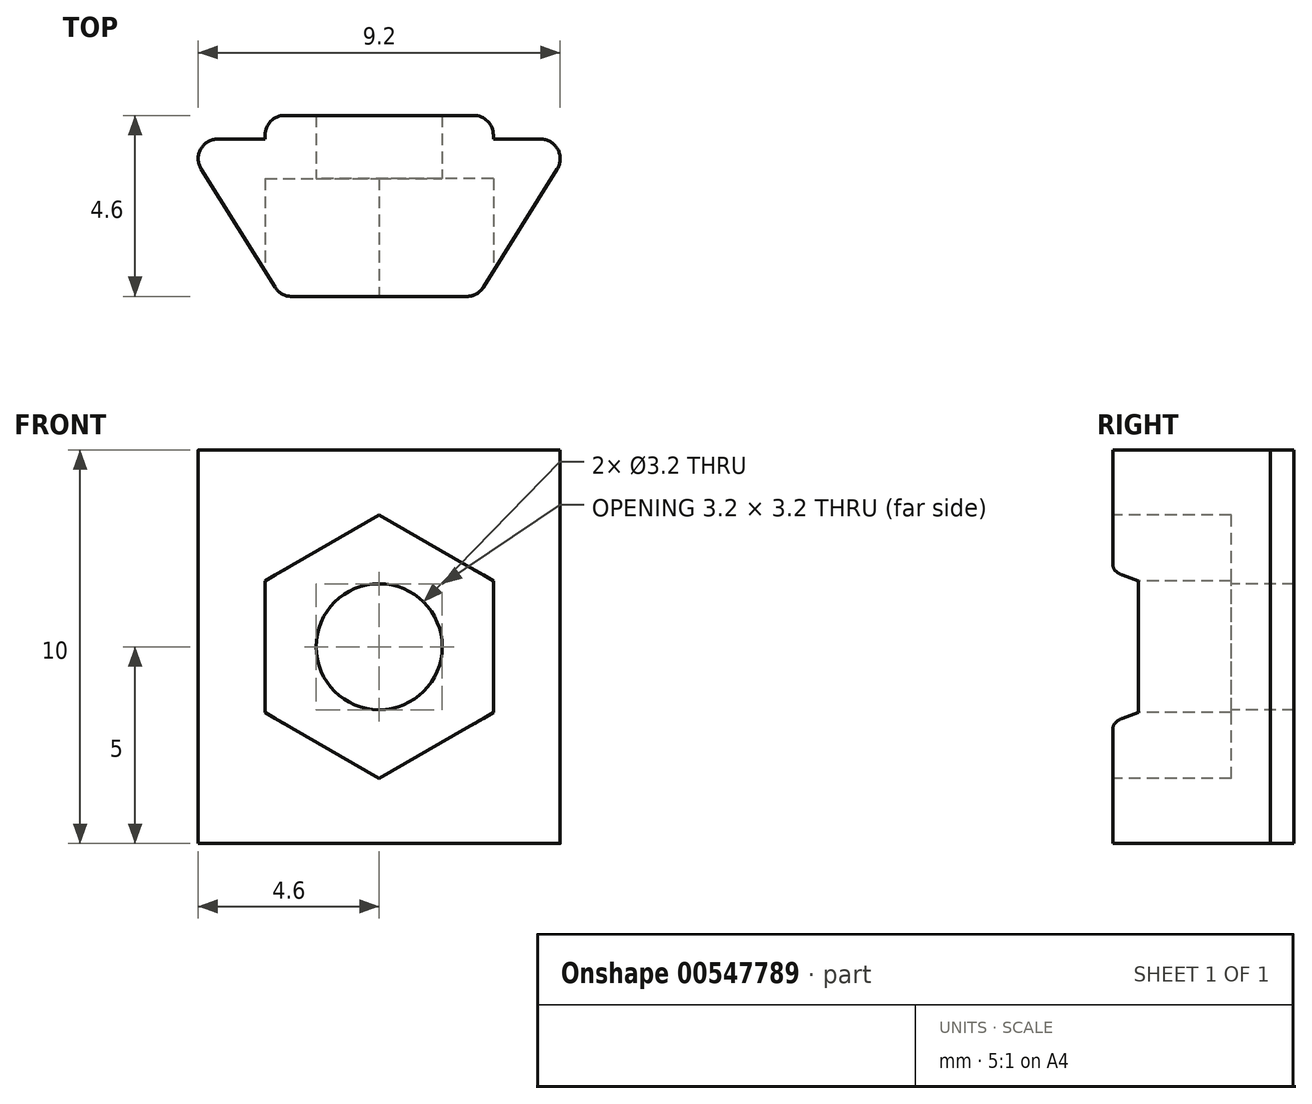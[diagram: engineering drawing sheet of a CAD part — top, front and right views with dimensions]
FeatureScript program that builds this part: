
annotation { "Feature Type Name" : "Feature", "Feature Type Description" : "" }
export const myFeature = defineFeature(function(context is Context, id is Id, definition is map)
    precondition{}
    {
        {
            var Q0;
            Q0=qCreatedBy(makeId("Top.planeOp"),FACE);
            var sketch = newSketch(context, id + "F0", { "sketchPlane" : qUnion([Q0])});
            skLineSegment(sketch, "E0.bottom", {"start": v(5, -2) * mm, "end": v(-5, -2) * mm, "construction": true});
            skLineSegment(sketch, "E0.top", {"start": v(5, 2) * mm, "end": v(-5, 2) * mm, "construction": true});
            skLineSegment(sketch, "E0.left", {"start": v(5, -2) * mm, "end": v(5, 2) * mm, "construction": true});
            skLineSegment(sketch, "E0.right", {"start": v(-5, -2) * mm, "end": v(-5, 2) * mm, "construction": true});
            skPoint(sketch, "E0.middle", {"position": v(0, 0) * mm});
            skLineSegment(sketch, "E1.bottom", {"start": v(2.9, 2.6) * mm, "end": v(-2.9, 2.6) * mm, "construction": true});
            skLineSegment(sketch, "E1.top", {"start": v(2.9, 1.4) * mm, "end": v(-2.9, 1.4) * mm, "construction": true});
            skLineSegment(sketch, "E1.left", {"start": v(2.9, 2.6) * mm, "end": v(2.9, 1.4) * mm, "construction": true});
            skLineSegment(sketch, "E1.right", {"start": v(-2.9, 2.6) * mm, "end": v(-2.9, 1.4) * mm, "construction": true});
            skPoint(sketch, "E1.middle", {"position": v(0, 2) * mm});
            skLineSegment(sketch, "E2", {"start": v(-5, 2) * mm, "end": v(-2.5, -2) * mm});
            skLineSegment(sketch, "E3", {"start": v(5, 2) * mm, "end": v(2.5, -2) * mm});
            skLineSegment(sketch, "E4", {"start": v(-2.5, -2) * mm, "end": v(2.5, -2) * mm});
            skLineSegment(sketch, "E5", {"start": v(-5, 2) * mm, "end": v(-2.9, 2) * mm});
            skLineSegment(sketch, "E6", {"start": v(-2.9, 2) * mm, "end": v(-2.9, 2.6) * mm});
            skLineSegment(sketch, "E7", {"start": v(-2.9, 2.6) * mm, "end": v(2.9, 2.6) * mm});
            skLineSegment(sketch, "E8", {"start": v(2.9, 2.6) * mm, "end": v(2.9, 2) * mm});
            skLineSegment(sketch, "E9", {"start": v(2.9, 2) * mm, "end": v(5, 2) * mm});
            skSolve(sketch);
        }
        {
            var Q0;
            Q0=qSketchRegion(id+"F0",true);
            extrude(context, id + "F1", {"entities" : qUnion([Q0]), "depth" : 10 * mm});
        }
        {
            var Q0;
            Q0=makeQuery(id+"F1.opExtrude","SWEPT_FACE",FACE,{"disambiguationData":[OSD([sQuery(id+"F0.wireOp",EDGE,"E4")])]});
            var sketch = newSketch(context, id + "F2", { "sketchPlane" : qUnion([Q0])});
            skCircle(sketch, "E10.cCircle", {"center": v(0, 5) * mm, "radius": 2.9 * mm, "construction": true});
            skPoint(sketch, "E10.cCircle.centerSnap0", {"position": v(2.5, 5) * mm});
            skPoint(sketch, "E10.cCircle.centerSnap1", {"position": v(0, 10) * mm});
            skLineSegment(sketch, "E10.0", {"start": v(2.9, 3.33) * mm, "end": v(0, 1.65) * mm});
            skLineSegment(sketch, "E10.1", {"start": v(0, 1.65) * mm, "end": v(-2.9, 3.33) * mm});
            skLineSegment(sketch, "E10.2", {"start": v(-2.9, 3.33) * mm, "end": v(-2.9, 6.67) * mm});
            skLineSegment(sketch, "E10.3", {"start": v(-2.9, 6.67) * mm, "end": v(0, 8.35) * mm});
            skLineSegment(sketch, "E10.4", {"start": v(0, 8.35) * mm, "end": v(2.9, 6.67) * mm});
            skLineSegment(sketch, "E10.5", {"start": v(2.9, 6.67) * mm, "end": v(2.9, 3.33) * mm});
            skPoint(sketch, "E10.0.midPoint", {"position": v(1.45, 2.49) * mm});
            skCircle(sketch, "E11", {"center": v(0, 5) * mm, "radius": 1.6 * mm});
            skSolve(sketch);
        }
        {
            var Q0;
            Q0=makeQuery(id+"F2.imprint","IMPRINT",FACE,{"disambiguationData":[TD([[makeQuery(id+"F2.imprint","IMPRINT",EDGE,{"derivedFrom":sQuery(id+"F2.wireOp",EDGE,"E11")}),1.0]])]});
            extrude(context, id + "F3", {"entities" : qUnion([Q0]), "operationType" : NewBodyOperationType.REMOVE, "endBound" : BoundingType.THROUGH_ALL, "oppositeDirection" : true, "depth" : 25 * mm});
        }
        {
            var Q0;
            Q0=makeQuery(id+"F2.imprint","IMPRINT",FACE,{"disambiguationData":[TD([[makeQuery(id+"F2.imprint","IMPRINT",EDGE,{"derivedFrom":sQuery(id+"F2.wireOp",EDGE,"E11")}),-1.0]])]});
            var Q1;
            {var subQ0=sQuery(id+"F2.wireOp",EDGE,"E10.5");Q1=makeQuery(id+"F2.imprint","IMPRINT",FACE,{"disambiguationData":[TD([[makeQuery(id+"F2.imprint","IMPRINT",EDGE,{"derivedFrom":subQ0}),-1.0]])]});}
            var Q2;
            {var subQ0=sQuery(id+"F2.wireOp",EDGE,"E10.2");Q2=makeQuery(id+"F2.imprint","IMPRINT",FACE,{"disambiguationData":[TD([[makeQuery(id+"F2.imprint","IMPRINT",EDGE,{"derivedFrom":subQ0}),-1.0]])]});}
            extrude(context, id + "F4", {"entities" : qUnion([Q0, Q1, Q2]), "operationType" : NewBodyOperationType.REMOVE, "oppositeDirection" : true, "depth" : 3 * mm});
        }
        {
            var Q0;
            Q0=makeQuery(id+"F1.opExtrude","SWEPT_EDGE",EDGE,{"disambiguationData":[OSD([sQuery(id+"F0.wireOp",EDGE,"E2"),sQuery(id+"F0.wireOp",EDGE,"E5")])]});
            var Q1;
            {var subQ0=sQuery(id+"F0.wireOp",EDGE,"E2");var subQ1=sQuery(id+"F0.wireOp",EDGE,"E4");Q1=makeQuery(id+"F4.boolean.opBoolean","SPLIT",EDGE,{"disambiguationData":[TD([makeQuery(id+"F4.opExtrude","SWEPT_FACE",FACE,{"disambiguationData":[OSD([sQuery(id+"F2.wireOp",EDGE,"E10.3")])]})])],"derivedFrom":makeQuery(id+"F1.opExtrude","SWEPT_EDGE",EDGE,{"disambiguationData":[OSD([subQ0,subQ1])]})});}
            var Q2;
            {var subQ0=sQuery(id+"F0.wireOp",EDGE,"E2");var subQ1=sQuery(id+"F0.wireOp",EDGE,"E4");Q2=makeQuery(id+"F4.boolean.opBoolean","SPLIT",EDGE,{"disambiguationData":[TD([makeQuery(id+"F4.opExtrude","SWEPT_FACE",FACE,{"disambiguationData":[OSD([sQuery(id+"F2.wireOp",EDGE,"E10.1")])]})])],"derivedFrom":makeQuery(id+"F1.opExtrude","SWEPT_EDGE",EDGE,{"disambiguationData":[OSD([subQ0,subQ1])]})});}
            var Q3;
            {var subQ0=sQuery(id+"F0.wireOp",EDGE,"E4");var subQ1=sQuery(id+"F0.wireOp",EDGE,"E3");Q3=makeQuery(id+"F4.boolean.opBoolean","SPLIT",EDGE,{"disambiguationData":[TD([makeQuery(id+"F4.opExtrude","SWEPT_FACE",FACE,{"disambiguationData":[OSD([sQuery(id+"F2.wireOp",EDGE,"E10.4")])]})])],"derivedFrom":makeQuery(id+"F1.opExtrude","SWEPT_EDGE",EDGE,{"disambiguationData":[OSD([subQ1,subQ0])]})});}
            var Q4;
            {var subQ0=sQuery(id+"F0.wireOp",EDGE,"E4");var subQ1=sQuery(id+"F0.wireOp",EDGE,"E3");Q4=makeQuery(id+"F4.boolean.opBoolean","SPLIT",EDGE,{"disambiguationData":[TD([makeQuery(id+"F4.opExtrude","SWEPT_FACE",FACE,{"disambiguationData":[OSD([sQuery(id+"F2.wireOp",EDGE,"E10.0")])]})])],"derivedFrom":makeQuery(id+"F1.opExtrude","SWEPT_EDGE",EDGE,{"disambiguationData":[OSD([subQ1,subQ0])]})});}
            var Q5;
            Q5=makeQuery(id+"F1.opExtrude","SWEPT_EDGE",EDGE,{"disambiguationData":[OSD([sQuery(id+"F0.wireOp",EDGE,"E3"),sQuery(id+"F0.wireOp",EDGE,"E9")])]});
            var Q6;
            Q6=makeQuery(id+"F1.opExtrude","SWEPT_EDGE",EDGE,{"disambiguationData":[OSD([sQuery(id+"F0.wireOp",EDGE,"E6"),sQuery(id+"F0.wireOp",EDGE,"E7")])]});
            var Q7;
            Q7=makeQuery(id+"F1.opExtrude","SWEPT_EDGE",EDGE,{"disambiguationData":[OSD([sQuery(id+"F0.wireOp",EDGE,"E7"),sQuery(id+"F0.wireOp",EDGE,"E8")])]});
            fillet(context, id + "F5", {"entities" : qUnion([Q0, Q1, Q2, Q3, Q4, Q5, Q6, Q7]), "radius" : 0.5 * mm, "tangentPropagation" : true, "allowEdgeOverflow" : false});
        }
    });
